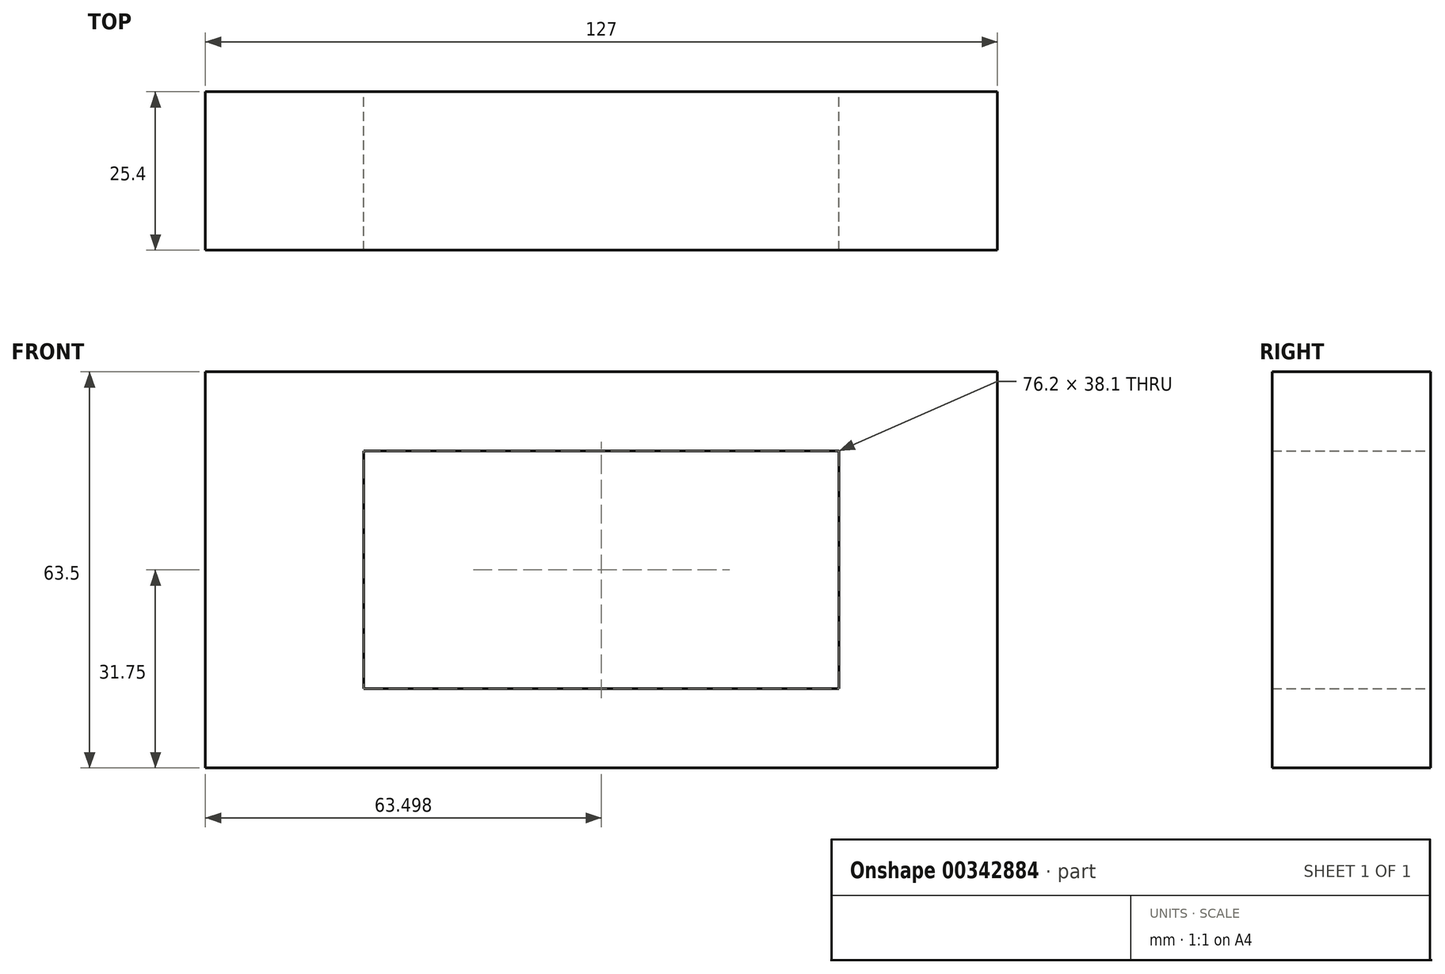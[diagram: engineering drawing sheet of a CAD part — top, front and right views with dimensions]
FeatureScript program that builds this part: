
annotation { "Feature Type Name" : "Feature", "Feature Type Description" : "" }
export const myFeature = defineFeature(function(context is Context, id is Id, definition is map)
    precondition{}
    {
        {
            var Q0;
            Q0=qCreatedBy(makeId("Front.planeOp"),FACE);
            var sketch = newSketch(context, id + "F0", { "sketchPlane" : qUnion([Q0])});
            skLineSegment(sketch, "E0.bottom", {"start": v(-109.23, 0) * mm, "end": v(17.77, 0) * mm});
            skLineSegment(sketch, "E0.top", {"start": v(-109.23, 63.5) * mm, "end": v(17.77, 63.5) * mm});
            skLineSegment(sketch, "E0.left", {"start": v(-109.23, 0) * mm, "end": v(-109.23, 63.5) * mm});
            skLineSegment(sketch, "E0.right", {"start": v(17.77, 0) * mm, "end": v(17.77, 63.5) * mm});
            skLineSegment(sketch, "E1.bottom", {"start": v(-83.83, 12.7) * mm, "end": v(-7.63, 12.7) * mm});
            skLineSegment(sketch, "E1.top", {"start": v(-83.83, 50.8) * mm, "end": v(-7.63, 50.8) * mm});
            skLineSegment(sketch, "E1.left", {"start": v(-83.83, 12.7) * mm, "end": v(-83.83, 50.8) * mm});
            skLineSegment(sketch, "E1.right", {"start": v(-7.63, 12.7) * mm, "end": v(-7.63, 50.8) * mm});
            skSolve(sketch);
        }
        {
            var Q0;
            Q0 = qSketchRegion(id + "F0", true);
            extrude(context, id + "F1", {"entities" : qUnion([Q0]), "depth" : 25.4 * mm});
        }
    });
